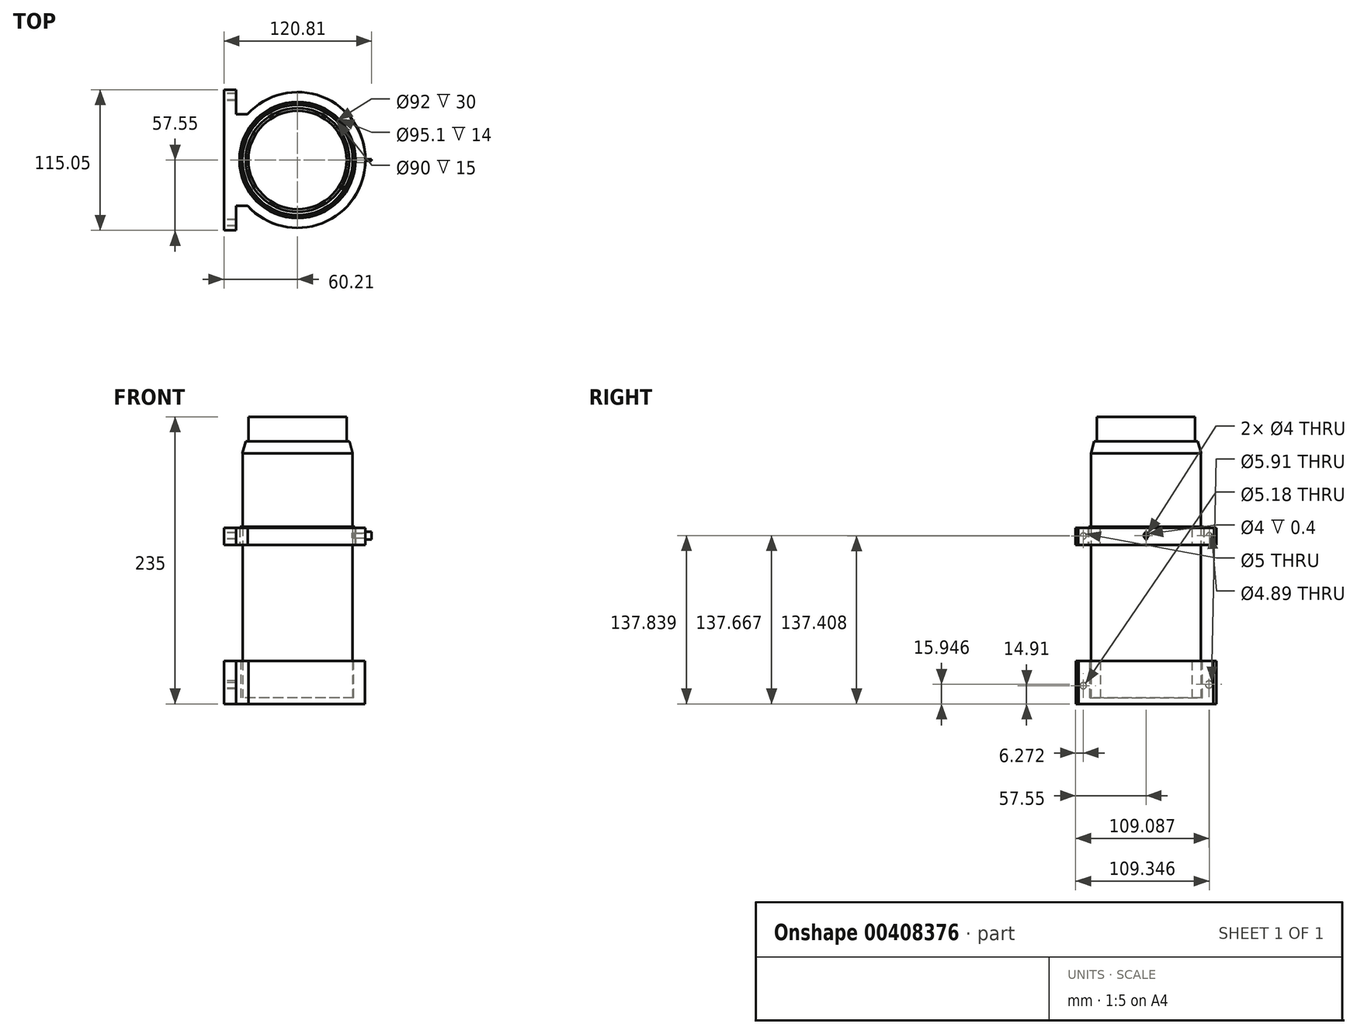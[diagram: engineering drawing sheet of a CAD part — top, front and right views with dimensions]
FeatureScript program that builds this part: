
annotation { "Feature Type Name" : "Feature", "Feature Type Description" : "" }
export const myFeature = defineFeature(function(context is Context, id is Id, definition is map)
    precondition{}
    {
        {
            var Q0;
            Q0=qCreatedBy(makeId("Top.planeOp"),FACE);
            var sketch = newSketch(context, id + "F0", { "sketchPlane" : qUnion([Q0])});
            skCircle(sketch, "E0", {"center": v(0, 0) * mm, "radius": 55 * mm});
            skSolve(sketch);
        }
        {
            var Q0;
            Q0=qCreatedBy(makeId("Top.planeOp"),FACE);
            var sketch = newSketch(context, id + "F1", { "sketchPlane" : qUnion([Q0])});
            skLineSegment(sketch, "E1.bottom", {"start": v(-50.21, 57.5) * mm, "end": v(-60.21, 57.5) * mm});
            skLineSegment(sketch, "E1.top", {"start": v(-50.21, -57.5) * mm, "end": v(-60.21, -57.5) * mm});
            skLineSegment(sketch, "E1.left", {"start": v(-50.21, 57.5) * mm, "end": v(-50.21, -57.5) * mm});
            skLineSegment(sketch, "E1.right", {"start": v(-60.21, 57.5) * mm, "end": v(-60.21, -57.5) * mm});
            skPoint(sketch, "E1.middle", {"position": v(-55.21, 0) * mm});
            skSolve(sketch);
        }
        {
            var Q0;
            Q0=makeQuery(id+"F1.imprint","IMPRINT",FACE,{"disambiguationData":[TD([[makeQuery(id+"F1.imprint","IMPRINT",EDGE,{"derivedFrom":sQuery(id+"F1.wireOp",EDGE,"E1.bottom")}),1.0]])]});
            extrude(context, id + "F2", {"entities" : qUnion([Q0]), "depth" : 35 * mm});
        }
        {
            var Q0;
            Q0=makeQuery(id+"F0.imprint","IMPRINT",FACE,{"disambiguationData":[TD([[makeQuery(id+"F0.imprint","IMPRINT",EDGE,{"derivedFrom":sQuery(id+"F0.wireOp",EDGE,"E0")}),1.0]])]});
            extrude(context, id + "F3", {"entities" : qUnion([Q0]), "operationType" : NewBodyOperationType.ADD, "depth" : 35 * mm});
        }
        {
            var Q0;
            Q0=qCreatedBy(makeId("Top.planeOp"),FACE);
            var sketch = newSketch(context, id + "F4", { "sketchPlane" : qUnion([Q0])});
            skLineSegment(sketch, "E2.0", {"start": v(-50.21, 57.5) * mm, "end": v(-60.21, 57.5) * mm, "construction": true});
            skLineSegment(sketch, "E3", {"start": v(-50.21, 57.5) * mm, "end": v(-50.21, 37.5) * mm, "construction": true});
            skLineSegment(sketch, "E4.0", {"start": v(-50.21, -57.5) * mm, "end": v(-60.21, -57.5) * mm, "construction": true});
            skLineSegment(sketch, "E5", {"start": v(-50.21, -57.5) * mm, "end": v(-50.21, -37.5) * mm, "construction": true});
            skSolve(sketch);
        }
        {
            var Q0;
            Q0=qCreatedBy(makeId("Top.planeOp"),FACE);
            var sketch = newSketch(context, id + "F5", { "sketchPlane" : qUnion([Q0])});
            skPoint(sketch, "E6.0", {"position": v(-50.21, 37.5) * mm});
            skLineSegment(sketch, "E7.0", {"start": v(-50.21, 57.5) * mm, "end": v(-50.21, 37.5) * mm});
            skLineSegment(sketch, "E8.bottom", {"start": v(-50.21, 37.5) * mm, "end": v(-40.21, 37.5) * mm});
            skLineSegment(sketch, "E8.top", {"start": v(-50.21, 21.5) * mm, "end": v(-40.21, 21.5) * mm});
            skLineSegment(sketch, "E8.left", {"start": v(-50.21, 37.5) * mm, "end": v(-50.21, 21.5) * mm});
            skLineSegment(sketch, "E8.right", {"start": v(-40.21, 37.5) * mm, "end": v(-40.21, 21.5) * mm});
            skPoint(sketch, "E9.0", {"position": v(-50.21, -37.5) * mm});
            skLineSegment(sketch, "E10.bottom", {"start": v(-50.21, -37.5) * mm, "end": v(-40.21, -37.5) * mm});
            skLineSegment(sketch, "E10.top", {"start": v(-50.21, -21.5) * mm, "end": v(-40.21, -21.5) * mm});
            skLineSegment(sketch, "E10.left", {"start": v(-50.21, -37.5) * mm, "end": v(-50.21, -21.5) * mm});
            skLineSegment(sketch, "E10.right", {"start": v(-40.21, -37.5) * mm, "end": v(-40.21, -21.5) * mm});
            skSolve(sketch);
        }
        {
            var Q0;
            Q0 = qSketchRegion(id + "F5", true);
            extrude(context, id + "F6", {"entities" : qUnion([Q0]), "operationType" : NewBodyOperationType.ADD, "depth" : 35 * mm});
        }
        {
            var Q0;
            Q0=makeQuery(id+"F6.boolean.opBoolean","MERGE",FACE,{"derivedFrom":[makeQuery(id+"F3.boolean.opBoolean","MERGE",FACE,{"derivedFrom":[makeQuery(id+"F2.opExtrude","CAP_FACE",FACE,{"disambiguationData":[OSD([sQuery(id+"F1.wireOp",EDGE,"E1.bottom"),sQuery(id+"F1.wireOp",EDGE,"E1.top"),sQuery(id+"F1.wireOp",EDGE,"E1.left"),sQuery(id+"F1.wireOp",EDGE,"E1.right")])],"isStart":false}),makeQuery(id+"F3.opExtrude","CAP_FACE",FACE,{"disambiguationData":[OSD([sQuery(id+"F0.wireOp",EDGE,"E0")])],"isStart":false})]}),makeQuery(id+"F6.opExtrude","CAP_FACE",FACE,{"disambiguationData":[OSD([sQuery(id+"F5.wireOp",EDGE,"E8.bottom"),sQuery(id+"F5.wireOp",EDGE,"E8.top"),sQuery(id+"F5.wireOp",EDGE,"E8.left"),sQuery(id+"F5.wireOp",EDGE,"E8.right")])],"isStart":false}),makeQuery(id+"F6.opExtrude","CAP_FACE",FACE,{"disambiguationData":[OSD([sQuery(id+"F5.wireOp",EDGE,"E10.bottom"),sQuery(id+"F5.wireOp",EDGE,"E10.top"),sQuery(id+"F5.wireOp",EDGE,"E10.left"),sQuery(id+"F5.wireOp",EDGE,"E10.right")])],"isStart":false})]});
            var sketch = newSketch(context, id + "F7", { "sketchPlane" : qUnion([Q0])});
            skCircle(sketch, "E11", {"center": v(0, 0) * mm, "radius": 46 * mm});
            skSolve(sketch);
        }
        {
            var Q0;
            Q0=makeQuery(id+"F7.imprint","IMPRINT",FACE,{"disambiguationData":[TD([[makeQuery(id+"F7.imprint","IMPRINT",EDGE,{"derivedFrom":sQuery(id+"F7.wireOp",EDGE,"E11")}),1.0]])]});
            extrude(context, id + "F8", {"entities" : qUnion([Q0]), "operationType" : NewBodyOperationType.REMOVE, "oppositeDirection" : true, "depth" : 30 * mm});
        }
        {
            var Q0;
            Q0=makeQuery(id+"F8.boolean.opBoolean","COPY",FACE,{"derivedFrom":makeQuery(id+"F8.opExtrude","CAP_FACE",FACE,{"disambiguationData":[OSD([sQuery(id+"F7.wireOp",EDGE,"E11")])],"isStart":false})});
            var sketch = newSketch(context, id + "F9", { "sketchPlane" : qUnion([Q0])});
            skCircle(sketch, "E12", {"center": v(0, 0) * mm, "radius": 45 * mm});
            skSolve(sketch);
        }
        {
            var Q0;
            Q0 = qSketchRegion(id + "F9", true);
            extrude(context, id + "F10", {"entities" : qUnion([Q0]), "depth" : 200 * mm});
        }
        {
            var Q0;
            Q0=makeQuery(id+"F10.opExtrude","CAP_FACE",FACE,{"disambiguationData":[OSD([sQuery(id+"F9.wireOp",EDGE,"E12")])],"isStart":false});
            cPlane(context, id + "F11", {"entities" : qUnion([Q0]), "cplaneType" : CPlaneType.OFFSET, "offset" : 75 * mm, "oppositeDirection" : true, "width" : 150 * mm, "height" : 150 * mm});
        }
        {
            var Q0;
            Q0=qCreatedBy(id+"F11.planeOp",FACE);
            var sketch = newSketch(context, id + "F12", { "sketchPlane" : qUnion([Q0])});
            skCircle(sketch, "E13", {"center": v(0, 0) * mm, "radius": 45 * mm});
            skCircle(sketch, "E14", {"center": v(0, 0) * mm, "radius": 47 * mm});
            skSolve(sketch);
        }
        {
            var Q0;
            Q0 = qSketchRegion(id + "F12", true);
            extrude(context, id + "F13", {"entities" : qUnion([Q0]), "depth" : 15 * mm});
        }
        {
            var Q0;
            Q0=qCreatedBy(id+"F11.planeOp",FACE);
            var sketch = newSketch(context, id + "F14", { "sketchPlane" : qUnion([Q0])});
            skCircle(sketch, "E15", {"center": v(0, 0) * mm, "radius": 47.55 * mm});
            skCircle(sketch, "E16", {"center": v(0, 0) * mm, "radius": 55.52 * mm});
            skSolve(sketch);
        }
        {
            var Q0;
            Q0 = qSketchRegion(id + "F14", true);
            extrude(context, id + "F15", {"entities" : qUnion([Q0]), "depth" : 14 * mm});
        }
        {
            var Q0;
            Q0=qCreatedBy(id+"F11.planeOp",FACE);
            var sketch = newSketch(context, id + "F16", { "sketchPlane" : qUnion([Q0])});
            skLineSegment(sketch, "E17.bottom", {"start": v(-60.2, -57.55) * mm, "end": v(-50.16, -57.55) * mm});
            skLineSegment(sketch, "E17.top", {"start": v(-60.2, 57.49) * mm, "end": v(-50.16, 57.49) * mm});
            skLineSegment(sketch, "E17.left", {"start": v(-60.2, -57.55) * mm, "end": v(-60.2, 57.49) * mm});
            skLineSegment(sketch, "E17.right", {"start": v(-50.16, -57.55) * mm, "end": v(-50.16, 57.49) * mm});
            skLineSegment(sketch, "E18.bottom", {"start": v(-50.16, -37.58) * mm, "end": v(-42.86, -37.58) * mm});
            skLineSegment(sketch, "E18.top", {"start": v(-50.16, -22.98) * mm, "end": v(-42.86, -22.98) * mm});
            skLineSegment(sketch, "E18.left", {"start": v(-50.16, -37.58) * mm, "end": v(-50.16, -22.98) * mm});
            skLineSegment(sketch, "E18.right", {"start": v(-42.86, -37.58) * mm, "end": v(-42.86, -22.98) * mm});
            skLineSegment(sketch, "E19.bottom", {"start": v(-42.86, -37.58) * mm, "end": v(-40.13, -37.58) * mm});
            skLineSegment(sketch, "E19.top", {"start": v(-42.86, -34.48) * mm, "end": v(-40.13, -34.48) * mm});
            skLineSegment(sketch, "E19.left", {"start": v(-42.86, -37.58) * mm, "end": v(-42.86, -34.48) * mm});
            skLineSegment(sketch, "E19.right", {"start": v(-40.13, -37.58) * mm, "end": v(-40.13, -34.48) * mm});
            skLineSegment(sketch, "E20.bottom", {"start": v(-50.16, 37.42) * mm, "end": v(-43.87, 37.42) * mm});
            skLineSegment(sketch, "E20.top", {"start": v(-50.16, 23.28) * mm, "end": v(-43.87, 23.28) * mm});
            skLineSegment(sketch, "E20.left", {"start": v(-50.16, 37.42) * mm, "end": v(-50.16, 23.28) * mm});
            skLineSegment(sketch, "E20.right", {"start": v(-43.87, 37.42) * mm, "end": v(-43.87, 23.28) * mm});
            skLineSegment(sketch, "E21.bottom", {"start": v(-43.87, 37.42) * mm, "end": v(-40.13, 37.42) * mm});
            skLineSegment(sketch, "E21.top", {"start": v(-43.87, 33.68) * mm, "end": v(-40.13, 33.68) * mm});
            skLineSegment(sketch, "E21.left", {"start": v(-43.87, 37.42) * mm, "end": v(-43.87, 33.68) * mm});
            skLineSegment(sketch, "E21.right", {"start": v(-40.13, 37.42) * mm, "end": v(-40.13, 33.68) * mm});
            skSolve(sketch);
        }
        {
            var Q0;
            Q0 = qSketchRegion(id + "F16", true);
            extrude(context, id + "F17", {"entities" : qUnion([Q0]), "operationType" : NewBodyOperationType.ADD, "depth" : 14 * mm});
        }
        {
            var Q0;
            Q0=makeQuery(id+"F10.opExtrude","CAP_FACE",FACE,{"disambiguationData":[OSD([sQuery(id+"F9.wireOp",EDGE,"E12")])],"isStart":false});
            var sketch = newSketch(context, id + "F18", { "sketchPlane" : qUnion([Q0])});
            skCircle(sketch, "E22", {"center": v(0, 0) * mm, "radius": 45.12 * mm});
            skSolve(sketch);
        }
        {
            var Q0;
            Q0 = qSketchRegion(id + "F18", true);
            extrude(context, id + "F19", {"entities" : qUnion([Q0]), "depth" : 10 * mm, "hasDraft" : true, "draftAngle" : 15 * degree, "draftPullDirection" : true});
        }
        {
            var Q0;
            Q0=makeQuery(id+"F19.opExtrude","CAP_FACE",FACE,{"disambiguationData":[OSD([sQuery(id+"F18.wireOp",EDGE,"E22")])],"isStart":false});
            var sketch = newSketch(context, id + "F20", { "sketchPlane" : qUnion([Q0])});
            skCircle(sketch, "E23", {"center": v(0, 0) * mm, "radius": 40.18 * mm});
            skSolve(sketch);
        }
        {
            var Q0;
            Q0=makeQuery(id+"F20.imprint","IMPRINT",FACE,{"disambiguationData":[TD([[makeQuery(id+"F20.imprint","IMPRINT",EDGE,{"derivedFrom":sQuery(id+"F20.wireOp",EDGE,"E23")}),1.0]])]});
            var Q1;
            Q1=sQuery(id+"F20.wireOp",EDGE,"E23");
            extrude(context, id + "F21", {"entities" : qUnion([Q0]), "surfaceEntities" : qUnion([Q1]), "depth" : 20 * mm});
        }
        {
            var Q0;
            Q0=makeQuery(id+"F2.opExtrude","SWEPT_FACE",FACE,{"disambiguationData":[OSD([sQuery(id+"F1.wireOp",EDGE,"E1.right")])]});
            var sketch = newSketch(context, id + "F22", { "sketchPlane" : qUnion([Q0])});
            skCircle(sketch, "E24", {"center": v(51.28, 14.91) * mm, "radius": 2.59 * mm});
            skCircle(sketch, "E25", {"center": v(-51.54, 15.95) * mm, "radius": 2.95 * mm});
            skCircle(sketch, "E26", {"center": v(-51.8, 137.67) * mm, "radius": 2.44 * mm});
            skCircle(sketch, "E27", {"center": v(51.28, 137.4) * mm, "radius": 2.5 * mm});
            skSolve(sketch);
        }
        {
            var Q0;
            Q0 = qSketchRegion(id + "F22", true);
            extrude(context, id + "F23", {"entities" : qUnion([Q0]), "operationType" : NewBodyOperationType.REMOVE, "oppositeDirection" : true, "depth" : 25 * mm});
        }
        {
            var Q0;
            Q0 = qSketchRegion(id + "F22", true);
            extrude(context, id + "F24", {"entities" : qUnion([Q0]), "operationType" : NewBodyOperationType.REMOVE, "oppositeDirection" : true, "depth" : 15 * mm});
        }
        {
            var Q0;
            Q0=qCreatedBy(makeId("Right.planeOp"),FACE);
            cPlane(context, id + "F25", {"entities" : qUnion([Q0]), "cplaneType" : CPlaneType.OFFSET, "offset" : 55.6 * mm, "width" : 150 * mm, "height" : 150 * mm});
        }
        {
            var Q0;
            Q0=qCreatedBy(id+"F25.planeOp",FACE);
            var sketch = newSketch(context, id + "F26", { "sketchPlane" : qUnion([Q0])});
            skCircle(sketch, "E28", {"center": v(0, 137.84) * mm, "radius": 2 * mm});
            skSolve(sketch);
        }
        {
            var Q0;
            Q0=makeQuery(id+"F26.imprint","IMPRINT",FACE,{"disambiguationData":[TD([[makeQuery(id+"F26.imprint","IMPRINT",EDGE,{"derivedFrom":sQuery(id+"F26.wireOp",EDGE,"E28")}),1.0]])]});
            var Q1;
            Q1=sQuery(id+"F26.wireOp",EDGE,"E28");
            extrude(context, id + "F27", {"entities" : qUnion([Q0]), "operationType" : NewBodyOperationType.REMOVE, "surfaceEntities" : qUnion([Q1]), "oppositeDirection" : true, "depth" : 11 * mm});
        }
        {
            var Q0;
            Q0=qCreatedBy(id+"F25.planeOp",FACE);
            var sketch = newSketch(context, id + "F28", { "sketchPlane" : qUnion([Q0])});
            skCircle(sketch, "E29", {"center": v(0, 137.8) * mm, "radius": 1.85 * mm});
            skSolve(sketch);
        }
        {
            var Q0;
            Q0 = qSketchRegion(id + "F28", true);
            extrude(context, id + "F29", {"entities" : qUnion([Q0]), "oppositeDirection" : true, "depth" : 10 * mm});
        }
        {
            var Q0;
            Q0=makeQuery(id+"F29.opExtrude","CAP_FACE",FACE,{"disambiguationData":[OSD([sQuery(id+"F28.wireOp",EDGE,"E29")])],"isStart":true});
            var sketch = newSketch(context, id + "F30", { "sketchPlane" : qUnion([Q0])});
            skLineSegment(sketch, "E30.bottom", {"start": v(-0.64, 134.6) * mm, "end": v(0.64, 134.6) * mm});
            skLineSegment(sketch, "E30.top", {"start": v(-0.64, 141) * mm, "end": v(0.64, 141) * mm});
            skLineSegment(sketch, "E30.left", {"start": v(-0.64, 134.6) * mm, "end": v(-0.64, 141) * mm});
            skLineSegment(sketch, "E30.right", {"start": v(0.64, 134.6) * mm, "end": v(0.64, 141) * mm});
            skPoint(sketch, "E30.middle", {"position": v(0, 137.8) * mm});
            skSolve(sketch);
        }
        {
            var Q0;
            Q0 = qSketchRegion(id + "F30", true);
            extrude(context, id + "F31", {"entities" : qUnion([Q0]), "operationType" : NewBodyOperationType.ADD, "depth" : 5 * mm});
        }
    });
